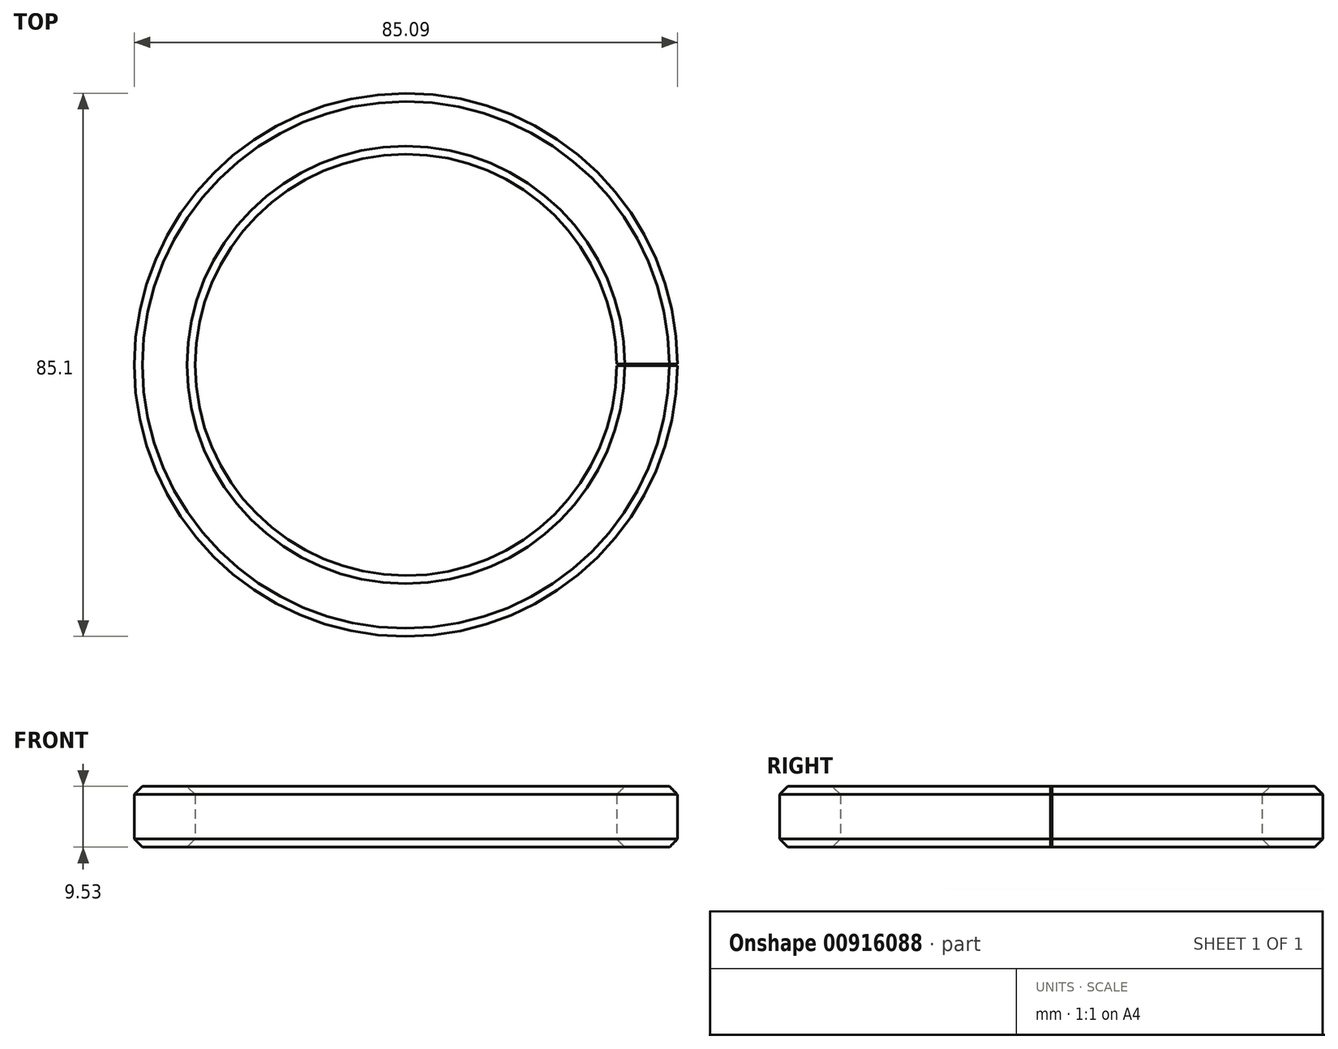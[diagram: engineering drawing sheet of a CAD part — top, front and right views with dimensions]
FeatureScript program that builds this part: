
annotation { "Feature Type Name" : "Feature", "Feature Type Description" : "" }
export const myFeature = defineFeature(function(context is Context, id is Id, definition is map)
    precondition{}
    {
        {
            var Q0;
            Q0=qCreatedBy(makeId("Top.planeOp"),FACE);
            var sketch = newSketch(context, id + "F0", { "sketchPlane" : qUnion([Q0])});
            skArc(sketch, "E0", {"start": v(33.02, 0.13) * mm, "mid": v(-33.02, 0) * mm, "end": v(33.02, -0.13) * mm});
            skArc(sketch, "E1.0", {"start": v(42.54, 0.13) * mm, "mid": v(-42.55, 0) * mm, "end": v(42.54, -0.13) * mm});
            skLineSegment(sketch, "E2.0", {"start": v(33.02, -0.13) * mm, "end": v(42.54, -0.13) * mm});
            skLineSegment(sketch, "E3.0", {"start": v(33.02, 0.13) * mm, "end": v(42.54, 0.13) * mm});
            skPoint(sketch, "E4.orphan", {"position": v(33.02, 0) * mm});
            skSolve(sketch);
        }
        {
            var Q0;
            Q0=makeQuery(id+"F0.imprint","IMPRINT",FACE,{"disambiguationData":[TD([[makeQuery(id+"F0.imprint","IMPRINT",EDGE,{"derivedFrom":sQuery(id+"F0.wireOp",EDGE,"E0")}),-1.0]])]});
            extrude(context, id + "F1", {"entities" : qUnion([Q0]), "depth" : 9.52 * mm, "offsetDistance" : 25.4 * mm});
        }
        {
            var Q0;
            Q0=makeQuery(id+"F1.opExtrude","CAP_EDGE",EDGE,{"disambiguationData":[OSD([sQuery(id+"F0.wireOp",EDGE,"E1.0")])],"isStart":false});
            var Q1;
            Q1=makeQuery(id+"F1.opExtrude","CAP_EDGE",EDGE,{"disambiguationData":[OSD([sQuery(id+"F0.wireOp",EDGE,"E1.0")])],"isStart":true});
            var Q2;
            Q2=makeQuery(id+"F1.opExtrude","CAP_EDGE",EDGE,{"disambiguationData":[OSD([sQuery(id+"F0.wireOp",EDGE,"E0")])],"isStart":false});
            var Q3;
            Q3=makeQuery(id+"F1.opExtrude","CAP_EDGE",EDGE,{"disambiguationData":[OSD([sQuery(id+"F0.wireOp",EDGE,"E0")])],"isStart":true});
            chamfer(context, id + "F2", {"entities" : qUnion([Q0, Q1, Q2, Q3]), "width" : 1.27 * mm, "tangentPropagation" : true});
        }
    });
